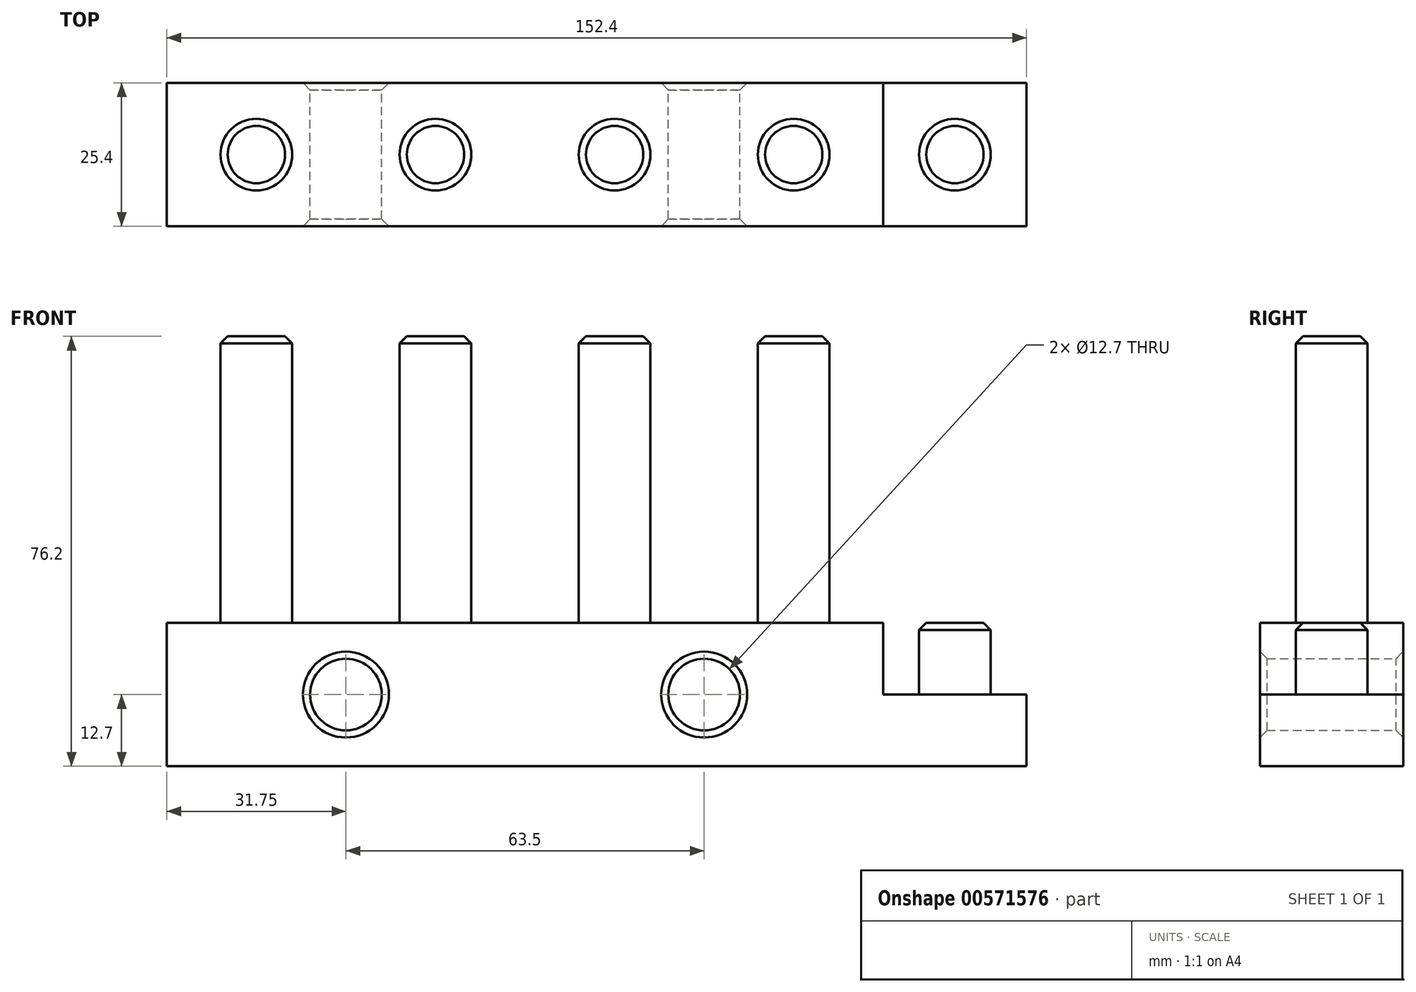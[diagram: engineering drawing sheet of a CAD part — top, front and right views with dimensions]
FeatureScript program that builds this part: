
annotation { "Feature Type Name" : "Feature", "Feature Type Description" : "" }
export const myFeature = defineFeature(function(context is Context, id is Id, definition is map)
    precondition{}
    {
        {
            var Q0;
            Q0=qCreatedBy(makeId("Front.planeOp"),FACE);
            var sketch = newSketch(context, id + "F0", { "sketchPlane" : qUnion([Q0])});
            skLineSegment(sketch, "E0", {"start": v(-127, -25.4) * mm, "end": v(0, -25.4) * mm});
            skLineSegment(sketch, "E1", {"start": v(0, -25.4) * mm, "end": v(0, 0) * mm});
            skLineSegment(sketch, "E2", {"start": v(0, 0) * mm, "end": v(-127, 0) * mm});
            skLineSegment(sketch, "E3", {"start": v(-127, 0) * mm, "end": v(-127, -25.4) * mm});
            skLineSegment(sketch, "E4", {"start": v(-63.5, 0) * mm, "end": v(-63.5, -25.4) * mm, "construction": true});
            skLineSegment(sketch, "E5", {"start": v(-63.5, -25.4) * mm, "end": v(-63.5, -12.7) * mm, "construction": true});
            skLineSegment(sketch, "E6", {"start": v(-63.5, -12.7) * mm, "end": v(0, -12.7) * mm, "construction": true});
            skLineSegment(sketch, "E7", {"start": v(-63.5, -12.7) * mm, "end": v(-127, -12.7) * mm, "construction": true});
            skCircle(sketch, "E8", {"center": v(-95.25, -12.7) * mm, "radius": 6.35 * mm});
            skCircle(sketch, "E9", {"center": v(-31.75, -12.7) * mm, "radius": 6.35 * mm});
            skSolve(sketch);
        }
        {
            var Q0;
            Q0 = qSketchRegion(id + "F0", true);
            extrude(context, id + "F1", {"entities" : qUnion([Q0]), "endBound" : BoundingType.SYMMETRIC, "depth" : 25.4 * mm, "offsetDistance" : 25.4 * mm});
        }
        {
            var Q0;
            Q0=makeQuery(id+"F1.opExtrude","CAP_EDGE",EDGE,{"disambiguationData":[OSD([sQuery(id+"F0.wireOp",EDGE,"E8")])],"isStart":false});
            var Q1;
            Q1=makeQuery(id+"F1.opExtrude","CAP_EDGE",EDGE,{"disambiguationData":[OSD([sQuery(id+"F0.wireOp",EDGE,"E9")])],"isStart":false});
            var Q2;
            Q2=makeQuery(id+"F1.opExtrude","CAP_EDGE",EDGE,{"disambiguationData":[OSD([sQuery(id+"F0.wireOp",EDGE,"E8")])],"isStart":true});
            var Q3;
            Q3=makeQuery(id+"F1.opExtrude","CAP_EDGE",EDGE,{"disambiguationData":[OSD([sQuery(id+"F0.wireOp",EDGE,"E9")])],"isStart":true});
            chamfer(context, id + "F2", {"entities" : qUnion([Q0, Q1, Q2, Q3]), "width" : 1.27 * mm, "tangentPropagation" : true});
        }
        {
            var Q0;
            Q0=makeQuery(id+"F1.opExtrude","SWEPT_FACE",FACE,{"disambiguationData":[OSD([sQuery(id+"F0.wireOp",EDGE,"E1")])]});
            var sketch = newSketch(context, id + "F3", { "sketchPlane" : qUnion([Q0])});
            skLineSegment(sketch, "E10", {"start": v(-12.7, -19.05) * mm, "end": v(12.7, -19.05) * mm});
            skSolve(sketch);
        }
        {
            var Q0;
            {var subQ0=sQuery(id+"F3.wireOp",EDGE,"E10");Q0=makeQuery(id+"F3.imprint","IMPRINT",FACE,{"disambiguationData":[TD([[makeQuery(id+"F3.imprint","IMPRINT",EDGE,{"derivedFrom":subQ0}),-1.0]])]});}
            extrude(context, id + "F4", {"entities" : qUnion([Q0]), "operationType" : NewBodyOperationType.ADD, "depth" : 25.4 * mm, "offsetDistance" : 25.4 * mm});
        }
        {
            var Q0;
            Q0=makeQuery(id+"F4.opExtrude","SWEPT_FACE",FACE,{"disambiguationData":[OSD([sQuery(id+"F3.wireOp",EDGE,"E10")])]});
            var sketch = newSketch(context, id + "F5", { "sketchPlane" : qUnion([Q0])});
            skLineSegment(sketch, "E11", {"start": v(0, 0) * mm, "end": v(25.4, 0) * mm, "construction": true});
            skCircle(sketch, "E12", {"center": v(12.7, 0) * mm, "radius": 6.35 * mm});
            skSolve(sketch);
        }
        {
            var Q0;
            Q0 = qSketchRegion(id + "F5", true);
            extrude(context, id + "F6", {"entities" : qUnion([Q0]), "operationType" : NewBodyOperationType.ADD, "depth" : 19.05 * mm, "offsetDistance" : 25.4 * mm});
        }
        {
            var Q0;
            Q0=makeQuery(id+"F4.opExtrude","SWEPT_FACE",FACE,{"disambiguationData":[OSD([sQuery(id+"F3.wireOp",EDGE,"E10")])]});
            extrude(context, id + "F7", {"entities" : qUnion([Q0]), "operationType" : NewBodyOperationType.ADD, "depth" : 6.35 * mm, "offsetDistance" : 25.4 * mm});
        }
        {
            var Q0;
            Q0=makeQuery(id+"F6.opExtrude","CAP_EDGE",EDGE,{"disambiguationData":[OSD([sQuery(id+"F5.wireOp",EDGE,"E12")])],"isStart":false});
            chamfer(context, id + "F8", {"entities" : qUnion([Q0]), "width" : 1.27 * mm, "tangentPropagation" : true});
        }
        {
            var Q0;
            Q0=makeQuery(id+"F1.opExtrude","SWEPT_FACE",FACE,{"disambiguationData":[OSD([sQuery(id+"F0.wireOp",EDGE,"E2")])]});
            var sketch = newSketch(context, id + "F9", { "sketchPlane" : qUnion([Q0])});
            skLineSegment(sketch, "E13", {"start": v(0, 0) * mm, "end": v(-31.75, 0) * mm, "construction": true});
            skLineSegment(sketch, "E14", {"start": v(-31.75, 0) * mm, "end": v(-63.5, 0) * mm, "construction": true});
            skLineSegment(sketch, "E15", {"start": v(-63.5, 0) * mm, "end": v(-95.25, 0) * mm, "construction": true});
            skLineSegment(sketch, "E16", {"start": v(-95.25, 0) * mm, "end": v(-127, 0) * mm, "construction": true});
            skCircle(sketch, "E17", {"center": v(-15.88, 0) * mm, "radius": 6.35 * mm});
            skCircle(sketch, "E18", {"center": v(-47.62, 0) * mm, "radius": 6.35 * mm});
            skCircle(sketch, "E19", {"center": v(-79.38, 0) * mm, "radius": 6.35 * mm});
            skCircle(sketch, "E20", {"center": v(-111.12, 0) * mm, "radius": 6.35 * mm});
            skSolve(sketch);
        }
        {
            var Q0;
            Q0 = qSketchRegion(id + "F9", true);
            extrude(context, id + "F10", {"entities" : qUnion([Q0]), "operationType" : NewBodyOperationType.ADD, "depth" : 50.8 * mm, "offsetDistance" : 25.4 * mm});
        }
        {
            var Q0;
            Q0=makeQuery(id+"F10.opExtrude","CAP_EDGE",EDGE,{"disambiguationData":[OSD([sQuery(id+"F9.wireOp",EDGE,"E17")])],"isStart":false});
            var Q1;
            Q1=makeQuery(id+"F10.opExtrude","CAP_EDGE",EDGE,{"disambiguationData":[OSD([sQuery(id+"F9.wireOp",EDGE,"E18")])],"isStart":false});
            var Q2;
            Q2=makeQuery(id+"F10.opExtrude","CAP_EDGE",EDGE,{"disambiguationData":[OSD([sQuery(id+"F9.wireOp",EDGE,"E19")])],"isStart":false});
            var Q3;
            Q3=makeQuery(id+"F10.opExtrude","CAP_EDGE",EDGE,{"disambiguationData":[OSD([sQuery(id+"F9.wireOp",EDGE,"E20")])],"isStart":false});
            chamfer(context, id + "F11", {"entities" : qUnion([Q0, Q1, Q2, Q3]), "width" : 1.27 * mm, "tangentPropagation" : true});
        }
    });
